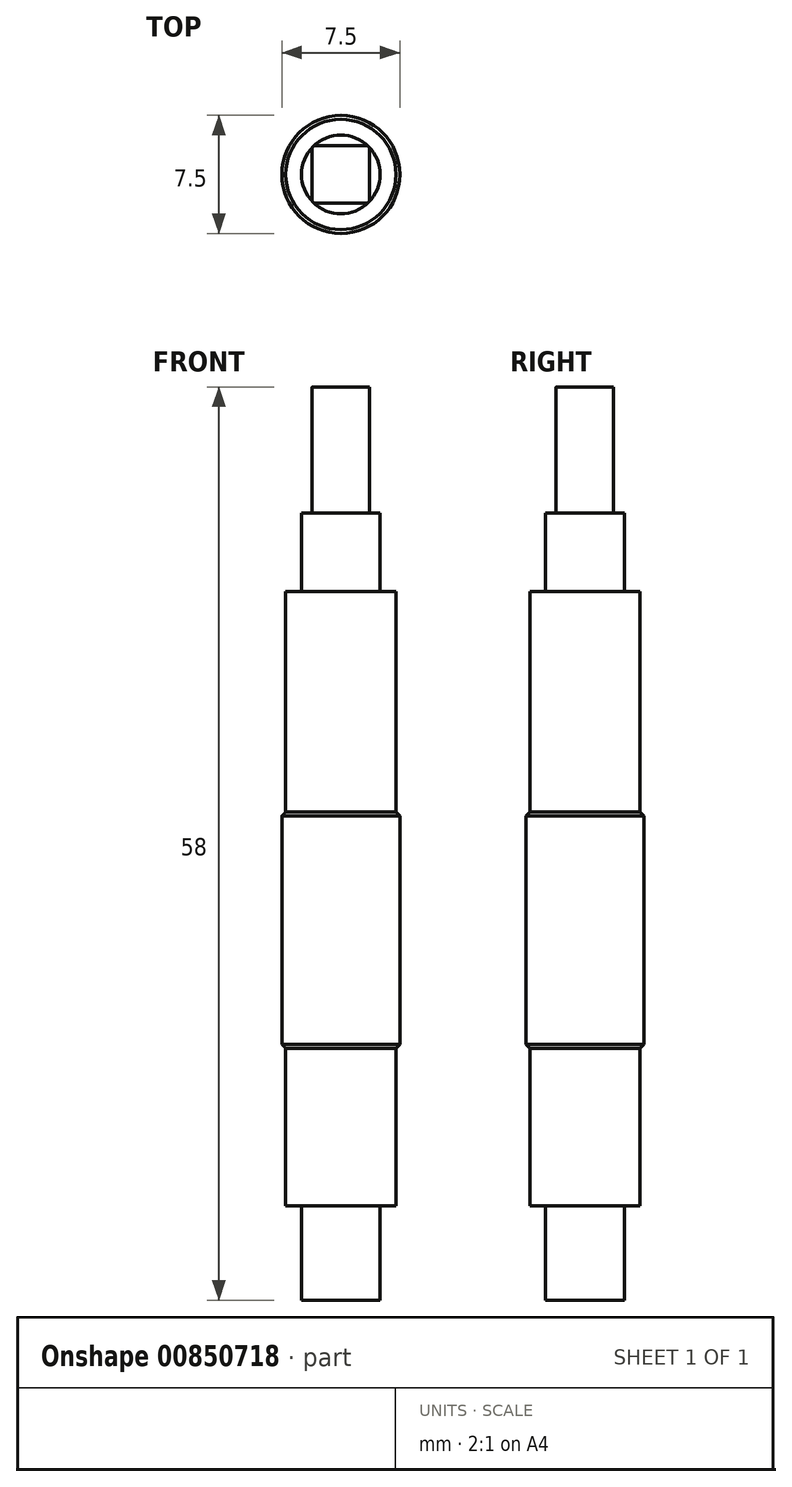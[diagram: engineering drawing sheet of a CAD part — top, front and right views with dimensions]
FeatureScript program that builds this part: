
annotation { "Feature Type Name" : "Feature", "Feature Type Description" : "" }
export const myFeature = defineFeature(function(context is Context, id is Id, definition is map)
    precondition{}
    {
        {
            var Q0;
            Q0=qCreatedBy(makeId("Top.planeOp"),FACE);
            var sketch = newSketch(context, id + "F0", { "sketchPlane" : qUnion([Q0])});
            skCircle(sketch, "E0", {"center": v(0, 0) * mm, "radius": 3.5 * mm});
            skSolve(sketch);
        }
        {
            var Q0;
            Q0=qSketchRegion(id+"F0",true);
            extrude(context, id + "F1", {"entities" : qUnion([Q0]), "depth" : 14 * mm, "offsetDistance" : 25 * mm});
        }
        {
            var Q0;
            Q0=makeQuery(id+"F1.opExtrude","CAP_FACE",FACE,{"disambiguationData":[OSD([sQuery(id+"F0.wireOp",EDGE,"E0")])],"isStart":false});
            var sketch = newSketch(context, id + "F2", { "sketchPlane" : qUnion([Q0])});
            skCircle(sketch, "E1", {"center": v(0, 0) * mm, "radius": 2.5 * mm});
            skSolve(sketch);
        }
        {
            var Q0;
            Q0=qSketchRegion(id+"F2",true);
            extrude(context, id + "F3", {"entities" : qUnion([Q0]), "operationType" : NewBodyOperationType.ADD, "depth" : 5 * mm, "offsetDistance" : 25 * mm});
        }
        {
            var Q0;
            Q0=makeQuery(id+"F3.opExtrude","CAP_FACE",FACE,{"disambiguationData":[OSD([sQuery(id+"F2.wireOp",EDGE,"E1")])],"isStart":false});
            var sketch = newSketch(context, id + "F4", { "sketchPlane" : qUnion([Q0])});
            skLineSegment(sketch, "E2.bottom", {"start": v(1.63, 1.83) * mm, "end": v(-1.63, 1.83) * mm});
            skLineSegment(sketch, "E2.top", {"start": v(1.63, -1.83) * mm, "end": v(-1.63, -1.83) * mm});
            skLineSegment(sketch, "E2.left", {"start": v(1.83, 1.63) * mm, "end": v(1.83, -1.63) * mm});
            skLineSegment(sketch, "E2.right", {"start": v(-1.83, 1.63) * mm, "end": v(-1.83, -1.63) * mm});
            skPoint(sketch, "E2.middle", {"position": v(0, 0) * mm});
            skPoint(sketch, "E3.visualSharp", {"position": v(-1.83, 1.83) * mm});
            skArc(sketch, "E3.filletArc", {"start": v(-1.63, 1.83) * mm, "mid": v(-1.77, 1.77) * mm, "end": v(-1.83, 1.63) * mm});
            skPoint(sketch, "E4.visualSharp", {"position": v(1.83, 1.83) * mm});
            skArc(sketch, "E4.filletArc", {"start": v(1.83, 1.63) * mm, "mid": v(1.77, 1.77) * mm, "end": v(1.63, 1.83) * mm});
            skPoint(sketch, "E5.visualSharp", {"position": v(1.83, -1.83) * mm});
            skArc(sketch, "E5.filletArc", {"start": v(1.63, -1.83) * mm, "mid": v(1.77, -1.77) * mm, "end": v(1.83, -1.63) * mm});
            skPoint(sketch, "E6.visualSharp", {"position": v(-1.83, -1.83) * mm});
            skArc(sketch, "E6.filletArc", {"start": v(-1.83, -1.63) * mm, "mid": v(-1.77, -1.77) * mm, "end": v(-1.63, -1.83) * mm});
            skSolve(sketch);
        }
        {
            var Q0;
            Q0=qSketchRegion(id+"F4",true);
            extrude(context, id + "F5", {"entities" : qUnion([Q0]), "operationType" : NewBodyOperationType.ADD, "depth" : 8 * mm, "offsetDistance" : 25 * mm});
        }
        {
            var Q0;
            Q0=makeQuery(id+"F1.opExtrude","CAP_FACE",FACE,{"disambiguationData":[OSD([sQuery(id+"F0.wireOp",EDGE,"E0")])],"isStart":true});
            var sketch = newSketch(context, id + "F6", { "sketchPlane" : qUnion([Q0])});
            skCircle(sketch, "E7", {"center": v(0, 0) * mm, "radius": 3.75 * mm});
            skSolve(sketch);
        }
        {
            var Q0;
            Q0 = qSketchRegion(id + "F6", true);
            extrude(context, id + "F7", {"entities" : qUnion([Q0]), "operationType" : NewBodyOperationType.ADD, "depth" : 15 * mm, "offsetDistance" : 25 * mm});
        }
        {
            var Q0;
            Q0=makeQuery(id+"F7.opExtrude","CAP_FACE",FACE,{"disambiguationData":[OSD([sQuery(id+"F6.wireOp",EDGE,"E7")])],"isStart":false});
            var sketch = newSketch(context, id + "F8", { "sketchPlane" : qUnion([Q0])});
            skCircle(sketch, "E8", {"center": v(0, 0) * mm, "radius": 3.5 * mm});
            skSolve(sketch);
        }
        {
            var Q0;
            Q0 = qSketchRegion(id + "F8", true);
            extrude(context, id + "F9", {"entities" : qUnion([Q0]), "operationType" : NewBodyOperationType.ADD, "depth" : 10 * mm, "offsetDistance" : 25 * mm});
        }
        {
            var Q0;
            Q0=makeQuery(id+"F7.opExtrude","CAP_EDGE",EDGE,{"disambiguationData":[OSD([sQuery(id+"F6.wireOp",EDGE,"E7")])],"isStart":true});
            var Q1;
            Q1=makeQuery(id+"F7.opExtrude","CAP_EDGE",EDGE,{"disambiguationData":[OSD([sQuery(id+"F6.wireOp",EDGE,"E7")])],"isStart":false});
            chamfer(context, id + "F10", {"entities" : qUnion([Q0, Q1]), "width" : 0.25 * mm, "tangentPropagation" : true});
        }
        {
            var Q0;
            Q0=makeQuery(id+"F9.opExtrude","CAP_FACE",FACE,{"disambiguationData":[OSD([sQuery(id+"F8.wireOp",EDGE,"E8")])],"isStart":false});
            var sketch = newSketch(context, id + "F11", { "sketchPlane" : qUnion([Q0])});
            skCircle(sketch, "E9", {"center": v(0, 0) * mm, "radius": 2.5 * mm});
            skSolve(sketch);
        }
        {
            var Q0;
            Q0 = qSketchRegion(id + "F11", true);
            extrude(context, id + "F12", {"entities" : qUnion([Q0]), "operationType" : NewBodyOperationType.ADD, "depth" : 6 * mm, "offsetDistance" : 25 * mm});
        }
    });
